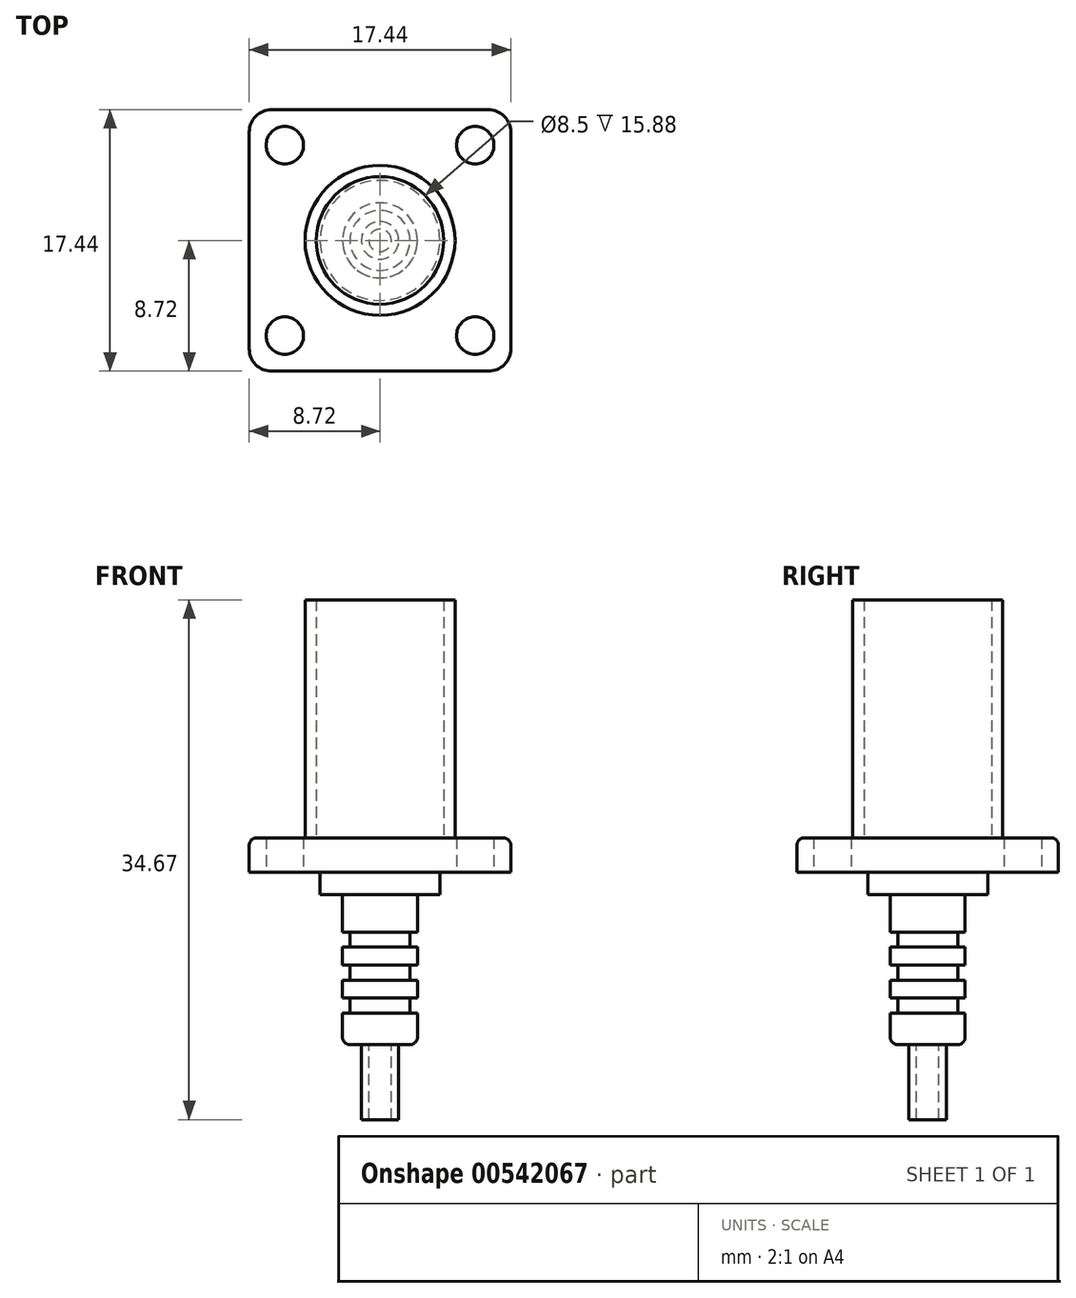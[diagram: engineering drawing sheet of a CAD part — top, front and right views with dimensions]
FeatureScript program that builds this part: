
annotation { "Feature Type Name" : "Feature", "Feature Type Description" : "" }
export const myFeature = defineFeature(function(context is Context, id is Id, definition is map)
    precondition{}
    {
        {
            var Q0;
            Q0=qCreatedBy(makeId("Top.planeOp"),FACE);
            var sketch = newSketch(context, id + "F0", { "sketchPlane" : qUnion([Q0])});
            skLineSegment(sketch, "E0.bottom", {"start": v(7.22, -8.72) * mm, "end": v(-7.23, -8.72) * mm});
            skLineSegment(sketch, "E0.top", {"start": v(7.23, 8.72) * mm, "end": v(-7.22, 8.72) * mm});
            skLineSegment(sketch, "E0.left", {"start": v(8.72, -7.22) * mm, "end": v(8.72, 7.23) * mm});
            skLineSegment(sketch, "E0.right", {"start": v(-8.72, -7.23) * mm, "end": v(-8.72, 7.22) * mm});
            skPoint(sketch, "E0.middle", {"position": v(0, 0) * mm});
            skPoint(sketch, "E1.visualSharp", {"position": v(-8.72, 8.72) * mm});
            skArc(sketch, "E1.filletArc", {"start": v(-7.22, 8.72) * mm, "mid": v(-8.29, 8.29) * mm, "end": v(-8.72, 7.22) * mm});
            skPoint(sketch, "E2.visualSharp", {"position": v(8.72, 8.72) * mm});
            skArc(sketch, "E2.filletArc", {"start": v(8.73, 7.23) * mm, "mid": v(8.29, 8.29) * mm, "end": v(7.23, 8.73) * mm});
            skPoint(sketch, "E3.visualSharp", {"position": v(8.72, -8.72) * mm});
            skArc(sketch, "E3.filletArc", {"start": v(7.22, -8.72) * mm, "mid": v(8.29, -8.29) * mm, "end": v(8.72, -7.22) * mm});
            skPoint(sketch, "E4.visualSharp", {"position": v(-8.72, -8.73) * mm});
            skArc(sketch, "E4.filletArc", {"start": v(-8.73, -7.23) * mm, "mid": v(-8.29, -8.29) * mm, "end": v(-7.23, -8.73) * mm});
            skCircle(sketch, "E5", {"center": v(6.35, 6.35) * mm, "radius": 1.25 * mm});
            skCircle(sketch, "E6", {"center": v(6.35, -6.35) * mm, "radius": 1.25 * mm});
            skCircle(sketch, "E7", {"center": v(-6.35, -6.35) * mm, "radius": 1.25 * mm});
            skCircle(sketch, "E8", {"center": v(-6.35, 6.35) * mm, "radius": 1.25 * mm});
            skSolve(sketch);
        }
        {
            var Q0;
            Q0 = qSketchRegion(id + "F0", true);
            extrude(context, id + "F1", {"entities" : qUnion([Q0]), "depth" : 2.3 * mm, "offsetDistance" : 25 * mm});
        }
        {
            var Q0;
            Q0=makeQuery(id+"F1.opExtrude","CAP_EDGE",EDGE,{"disambiguationData":[OSD([sQuery(id+"F0.wireOp",EDGE,"E0.bottom")])],"isStart":false});
            fillet(context, id + "F2", {"entities" : qUnion([Q0]), "radius" : .5 * mm, "tangentPropagation" : true, "allowEdgeOverflow" : false});
        }
        {
            var Q0;
            Q0=makeQuery(id+"F1.opExtrude","CAP_FACE",FACE,{"disambiguationData":[OSD([sQuery(id+"F0.wireOp",EDGE,"E0.bottom"),sQuery(id+"F0.wireOp",EDGE,"E0.top"),sQuery(id+"F0.wireOp",EDGE,"E0.left"),sQuery(id+"F0.wireOp",EDGE,"E0.right"),sQuery(id+"F0.wireOp",EDGE,"E1.filletArc"),sQuery(id+"F0.wireOp",EDGE,"E2.filletArc"),sQuery(id+"F0.wireOp",EDGE,"E3.filletArc"),sQuery(id+"F0.wireOp",EDGE,"E4.filletArc")])],"isStart":false});
            var sketch = newSketch(context, id + "F3", { "sketchPlane" : qUnion([Q0])});
            skCircle(sketch, "E9", {"center": v(0, 0) * mm, "radius": 5 * mm});
            skCircle(sketch, "E10", {"center": v(0, 0) * mm, "radius": 4.25 * mm});
            skSolve(sketch);
        }
        {
            var Q0;
            Q0 = qSketchRegion(id + "F3", true);
            extrude(context, id + "F4", {"entities" : qUnion([Q0]), "operationType" : NewBodyOperationType.ADD, "depth" : 15.88 * mm, "offsetDistance" : 25 * mm});
        }
        {
            var Q0;
            Q0=makeQuery(id+"F1.opExtrude","CAP_FACE",FACE,{"disambiguationData":[OSD([sQuery(id+"F0.wireOp",EDGE,"E0.bottom"),sQuery(id+"F0.wireOp",EDGE,"E0.top"),sQuery(id+"F0.wireOp",EDGE,"E0.left"),sQuery(id+"F0.wireOp",EDGE,"E0.right"),sQuery(id+"F0.wireOp",EDGE,"E1.filletArc"),sQuery(id+"F0.wireOp",EDGE,"E2.filletArc"),sQuery(id+"F0.wireOp",EDGE,"E3.filletArc"),sQuery(id+"F0.wireOp",EDGE,"E4.filletArc"),sQuery(id+"F0.wireOp",EDGE,"E5"),sQuery(id+"F0.wireOp",EDGE,"E6"),sQuery(id+"F0.wireOp",EDGE,"E7"),sQuery(id+"F0.wireOp",EDGE,"E8")])],"isStart":true});
            var sketch = newSketch(context, id + "F5", { "sketchPlane" : qUnion([Q0])});
            skCircle(sketch, "E11", {"center": v(0, 0) * mm, "radius": 4 * mm});
            skSolve(sketch);
        }
        {
            var Q0;
            Q0 = qSketchRegion(id + "F5", true);
            extrude(context, id + "F6", {"entities" : qUnion([Q0]), "operationType" : NewBodyOperationType.ADD, "depth" : 1.5 * mm, "offsetDistance" : 25 * mm});
        }
        {
            var Q0;
            Q0=makeQuery(id+"F6.opExtrude","CAP_FACE",FACE,{"disambiguationData":[OSD([sQuery(id+"F5.wireOp",EDGE,"E11")])],"isStart":false});
            var sketch = newSketch(context, id + "F7", { "sketchPlane" : qUnion([Q0])});
            skCircle(sketch, "E12", {"center": v(0, 0) * mm, "radius": 2.5 * mm});
            skSolve(sketch);
        }
        {
            var Q0;
            Q0 = qSketchRegion(id + "F7", true);
            extrude(context, id + "F8", {"entities" : qUnion([Q0]), "operationType" : NewBodyOperationType.ADD, "depth" : 10 * mm, "offsetDistance" : 25 * mm});
        }
        {
            var Q0;
            Q0=makeQuery(id+"F6.opExtrude","CAP_EDGE",EDGE,{"disambiguationData":[OSD([sQuery(id+"F5.wireOp",EDGE,"E11")])],"isStart":true});
            var Q1;
            Q1=makeQuery(id+"F8.opExtrude","CAP_EDGE",EDGE,{"disambiguationData":[OSD([sQuery(id+"F7.wireOp",EDGE,"E12")])],"isStart":false});
            fillet(context, id + "F9", {"entities" : qUnion([Q0, Q1]), "radius" : .5 * mm, "tangentPropagation" : true, "allowEdgeOverflow" : false});
        }
        {
            var Q0;
            Q0=qCreatedBy(makeId("Right.planeOp"),FACE);
            var sketch = newSketch(context, id + "F10", { "sketchPlane" : qUnion([Q0])});
            skLineSegment(sketch, "E13", {"start": v(-2, -4) * mm, "end": v(-2, -5) * mm});
            skLineSegment(sketch, "E14", {"start": v(-2, -5) * mm, "end": v(-3.5, -5) * mm});
            skLineSegment(sketch, "E15", {"start": v(-3.5, -5) * mm, "end": v(-3.5, -6.2) * mm});
            skLineSegment(sketch, "E16", {"start": v(-3.5, -6.2) * mm, "end": v(-2, -6.2) * mm});
            skLineSegment(sketch, "E17", {"start": v(-2, -6.2) * mm, "end": v(-2, -7.2) * mm});
            skLineSegment(sketch, "E18", {"start": v(-2, -7.2) * mm, "end": v(-3.5, -7.2) * mm});
            skLineSegment(sketch, "E19", {"start": v(-3.5, -7.2) * mm, "end": v(-3.5, -8.4) * mm});
            skLineSegment(sketch, "E20", {"start": v(-3.5, -8.4) * mm, "end": v(-2, -8.4) * mm});
            skLineSegment(sketch, "E21", {"start": v(-2, -8.4) * mm, "end": v(-2, -9.4) * mm});
            skLineSegment(sketch, "E22", {"start": v(-2, -9.4) * mm, "end": v(-6, -9.4) * mm});
            skLineSegment(sketch, "E23", {"start": v(-6, -9.4) * mm, "end": v(-6, -4) * mm});
            skLineSegment(sketch, "E24", {"start": v(-6, -4) * mm, "end": v(-2, -4) * mm});
            skLineSegment(sketch, "E25", {"start": v(0, 0) * mm, "end": v(0, -14.96) * mm, "construction": true});
            skSolve(sketch);
        }
        {
            var Q0;
            Q0=makeQuery(id+"F10.imprint","IMPRINT",FACE,{"disambiguationData":[TD([[makeQuery(id+"F10.imprint","IMPRINT",EDGE,{"derivedFrom":sQuery(id+"F10.wireOp",EDGE,"E13")}),-1.0]])]});
            var Q1;
            Q1=sQuery(id+"F10.wireOp",EDGE,"E25");
            revolve(context, id + "F11", {"operationType" : NewBodyOperationType.REMOVE, "entities" : qUnion([Q0]), "axis" : qUnion([Q1]), "revolveType" : RevolveType.FULL, "oppositeDirection" : true});
        }
        {
            var Q0;
            Q0=makeQuery(id+"F8.opExtrude","CAP_FACE",FACE,{"disambiguationData":[OSD([sQuery(id+"F7.wireOp",EDGE,"E12")])],"isStart":false});
            var sketch = newSketch(context, id + "F12", { "sketchPlane" : qUnion([Q0])});
            skCircle(sketch, "E26", {"center": v(0, 0) * mm, "radius": 1.25 * mm});
            skCircle(sketch, "E27", {"center": v(0, 0) * mm, "radius": 0.75 * mm});
            skSolve(sketch);
        }
        {
            var Q0;
            Q0 = qSketchRegion(id + "F12", true);
            extrude(context, id + "F13", {"entities" : qUnion([Q0]), "operationType" : NewBodyOperationType.ADD, "depth" : 5 * mm, "offsetDistance" : 25 * mm});
        }
    });
